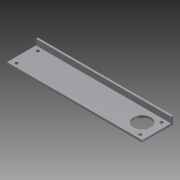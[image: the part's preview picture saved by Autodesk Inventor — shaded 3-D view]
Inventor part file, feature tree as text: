
AUTODESK INVENTOR PART (.ipt)
format: ipt  version: 2012 (Build 160160000, 160)  size: 102,400 bytes
history: native  units: in
note: dims shown in document units (in); Inventor stores cm internally (conversion verified against a paired STEP export)
features: extrude x3, sketch x2
ambient origin geometry x8: Origin, YZ Plane, XZ Plane, XY Plane, X Axis, Y Axis, Z Axis, Center Point
bodies: Solid1 (feature_tree)
feature tree (5):
  sketch  "Sketch1"  dims[d4=0.125in d6=0.125in]
  extrude  "Extrusion1"  Depth=0.125in
  extrude  "Extrusion2"  Depth=8.75in
  extrude  "Extrusion3"  Depth=0.125in TaperAngle=0.0deg
  sketch  "Sketch2"  dims[d9=0.5in d11=8.75in d14=0.125in d15=0.0in d16=2.0in d17=0.0in d22=1.0in d23=0.0in d26=1.0in d27=1.0in d28=1.125in d29=0.2in d30=0.375in d31=0.25in d32=0.375in d33=0.375in d34=0.25in d35=0.375in d36=0.375in d37=0.375in]
